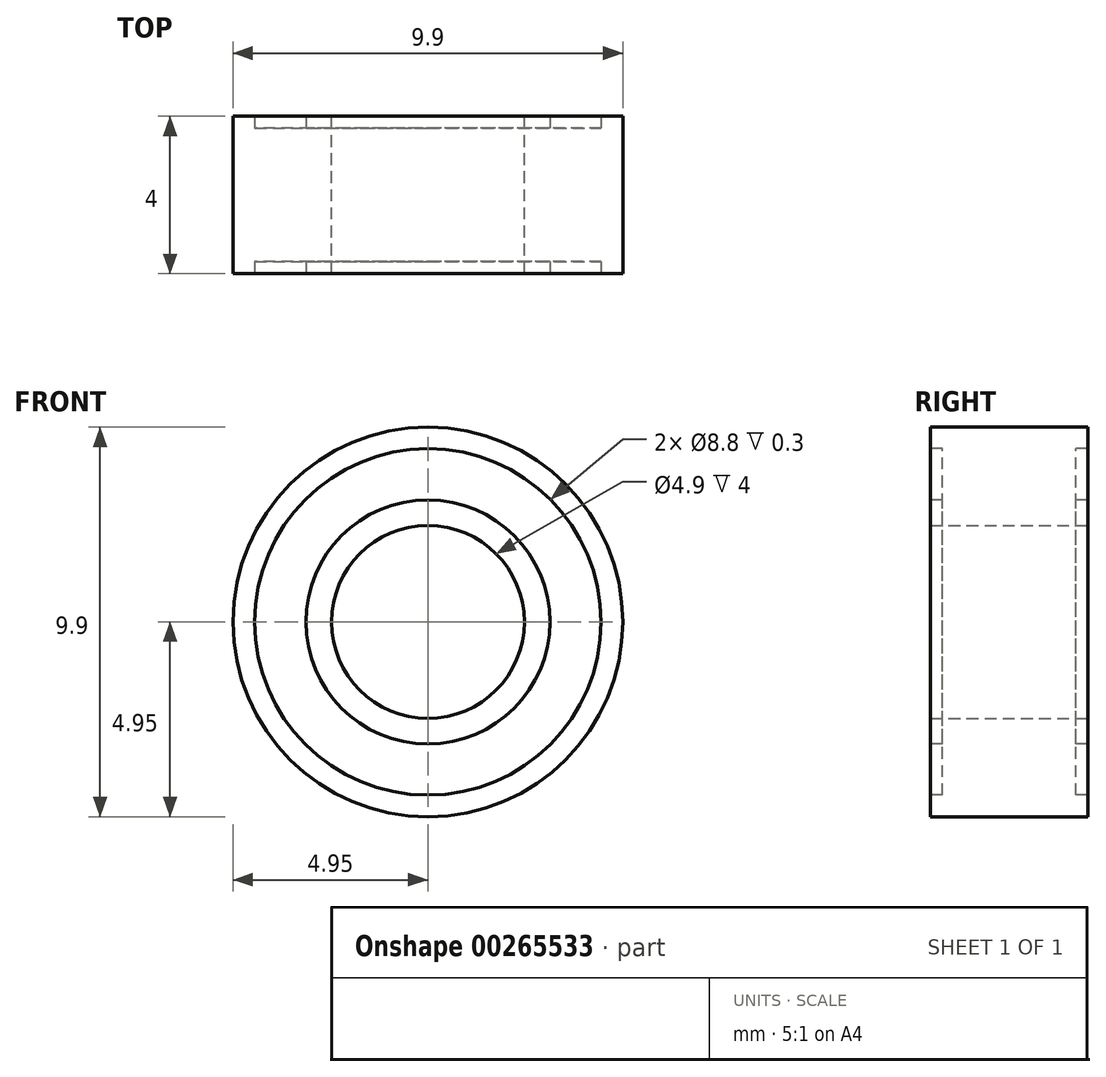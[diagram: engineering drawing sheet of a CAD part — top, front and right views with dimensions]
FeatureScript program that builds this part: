
annotation { "Feature Type Name" : "Feature", "Feature Type Description" : "" }
export const myFeature = defineFeature(function(context is Context, id is Id, definition is map)
    precondition{}
    {
        {
            var Q0;
            Q0=qCreatedBy(makeId("Front.planeOp"),FACE);
            var sketch = newSketch(context, id + "F0", { "sketchPlane" : qUnion([Q0])});
            skCircle(sketch, "E0", {"center": v(0, 0) * mm, "radius": 4.95 * mm});
            skCircle(sketch, "E1", {"center": v(0, 0) * mm, "radius": 2.45 * mm});
            skSolve(sketch);
        }
        {
            var Q0;
            Q0=makeQuery(id+"F0.imprint","IMPRINT",FACE,{"disambiguationData":[TD([[makeQuery(id+"F0.imprint","IMPRINT",EDGE,{"derivedFrom":sQuery(id+"F0.wireOp",EDGE,"E0")}),1.0]])]});
            extrude(context, id + "F1", {"entities" : qUnion([Q0]), "depth" : 4 * mm});
        }
        {
            var Q0;
            Q0=qCreatedBy(makeId("Right.planeOp"),FACE);
            var sketch = newSketch(context, id + "F2", { "sketchPlane" : qUnion([Q0])});
            skLineSegment(sketch, "E2", {"start": v(0, 0) * mm, "end": v(-2, 0) * mm, "construction": true});
            skLineSegment(sketch, "E3", {"start": v(0, 0) * mm, "end": v(0, 3.1) * mm, "construction": true});
            skLineSegment(sketch, "E4", {"start": v(0, 3.1) * mm, "end": v(-0.3, 3.1) * mm, "construction": true});
            skLineSegment(sketch, "E5", {"start": v(-0.3, 3.1) * mm, "end": v(-0.3, 4.4) * mm, "construction": true});
            skLineSegment(sketch, "E6", {"start": v(-0.3, 4.4) * mm, "end": v(0, 4.4) * mm, "construction": true});
            skLineSegment(sketch, "E7", {"start": v(0, 4.4) * mm, "end": v(0, 3.1) * mm, "construction": true});
            skLineSegment(sketch, "E8", {"start": v(-2, 0) * mm, "end": v(-2, 6.65) * mm, "construction": true});
            skLineSegment(sketch, "E9.MirrorCS", {"start": v(-4, 3.1) * mm, "end": v(-3.7, 3.1) * mm, "construction": true});
            skLineSegment(sketch, "E10.MirrorCS", {"start": v(-3.7, 4.4) * mm, "end": v(-4, 4.4) * mm, "construction": true});
            skLineSegment(sketch, "E11.MirrorCS", {"start": v(-3.7, 3.1) * mm, "end": v(-3.7, 4.4) * mm, "construction": true});
            skLineSegment(sketch, "E12.MirrorCS", {"start": v(-4, 4.4) * mm, "end": v(-4, 3.1) * mm, "construction": true});
            skLineSegment(sketch, "E13.left", {"start": v(-3.7, 4.4) * mm, "end": v(-3.7, 3.07) * mm});
            skLineSegment(sketch, "E14.bottom", {"start": v(-3.7, 3.07) * mm, "end": v(-3.7, 3.07) * mm});
            skLineSegment(sketch, "E14.top", {"start": v(-3.7, 3.1) * mm, "end": v(-3.7, 3.1) * mm});
            skLineSegment(sketch, "E14.left", {"start": v(-3.7, 3.07) * mm, "end": v(-3.7, 3.1) * mm});
            skLineSegment(sketch, "E14.right", {"start": v(-3.7, 3.07) * mm, "end": v(-3.7, 3.1) * mm});
            skLineSegment(sketch, "E15.left", {"start": v(-3.7, 3.1) * mm, "end": v(-3.7, 3.07) * mm});
            skLineSegment(sketch, "E15.right", {"start": v(-3.7, 3.1) * mm, "end": v(-3.7, 3.07) * mm});
            skLineSegment(sketch, "E16.bottom", {"start": v(-0.3, 4.4) * mm, "end": v(0.27, 4.4) * mm});
            skLineSegment(sketch, "E16.top", {"start": v(-0.3, 3.1) * mm, "end": v(0.27, 3.1) * mm});
            skLineSegment(sketch, "E16.left", {"start": v(-0.3, 4.4) * mm, "end": v(-0.3, 3.1) * mm});
            skLineSegment(sketch, "E16.right", {"start": v(0.27, 4.4) * mm, "end": v(0.27, 3.1) * mm});
            skLineSegment(sketch, "E17.bottom", {"start": v(-3.7, 4.4) * mm, "end": v(-4.42, 4.4) * mm});
            skLineSegment(sketch, "E17.top", {"start": v(-3.7, 3.1) * mm, "end": v(-4.42, 3.1) * mm});
            skLineSegment(sketch, "E17.left", {"start": v(-3.7, 4.4) * mm, "end": v(-3.7, 3.1) * mm});
            skLineSegment(sketch, "E17.right", {"start": v(-4.42, 4.4) * mm, "end": v(-4.42, 3.1) * mm});
            skSolve(sketch);
        }
        {
            var Q0;
            Q0=makeQuery(id+"F2.imprint","IMPRINT",FACE,{"disambiguationData":[TD([[makeQuery(id+"F2.imprint","IMPRINT",EDGE,{"derivedFrom":sQuery(id+"F2.wireOp",EDGE,"E17.bottom")}),1.0]])]});
            var Q1;
            Q1=makeQuery(id+"F2.imprint","IMPRINT",FACE,{"disambiguationData":[TD([[makeQuery(id+"F2.imprint","IMPRINT",EDGE,{"derivedFrom":sQuery(id+"F2.wireOp",EDGE,"E16.bottom")}),-1.0]])]});
            var Q2;
            Q2=sQuery(id+"F2.wireOp",EDGE,"E2");
            revolve(context, id + "F3", {"operationType" : NewBodyOperationType.REMOVE, "entities" : qUnion([Q0, Q1]), "axis" : qUnion([Q2]), "revolveType" : RevolveType.FULL, "oppositeDirection" : true});
        }
    });
